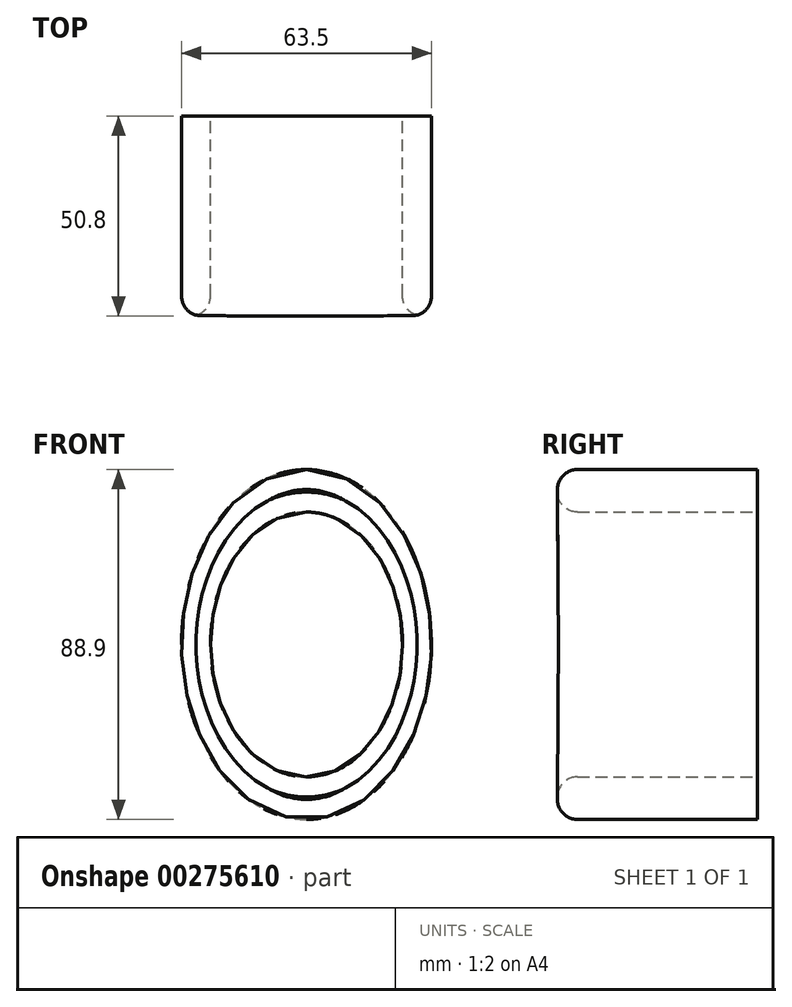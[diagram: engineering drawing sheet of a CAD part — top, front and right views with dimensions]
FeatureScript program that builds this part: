
annotation { "Feature Type Name" : "Feature", "Feature Type Description" : "" }
export const myFeature = defineFeature(function(context is Context, id is Id, definition is map)
    precondition{}
    {
        {
            var Q0;
            Q0=qCreatedBy(makeId("Front.planeOp"),FACE);
            var sketch = newSketch(context, id + "F0", { "sketchPlane" : qUnion([Q0])});
            skEllipse(sketch, "E0", {"center": v(0, 0) * mm, "majorRadius": 44.45 * mm, "minorRadius": 31.75 * mm, "majorAxis": v(0, 1)});
            skEllipse(sketch, "E1", {"center": v(0, 0) * mm, "majorRadius": 33.64 * mm, "minorRadius": 24.39 * mm, "majorAxis": v(0, 1)});
            skSolve(sketch);
        }
        {
            var Q0;
            Q0 = qSketchRegion(id + "F0", true);
            extrude(context, id + "F1", {"entities" : qUnion([Q0]), "depth" : 50.8 * mm});
        }
        {
            var Q0;
            Q0=makeQuery(id+"F1.opExtrude","CAP_EDGE",EDGE,{"disambiguationData":[OSD([sQuery(id+"F0.wireOp",EDGE,"E1")])],"isStart":false});
            var Q1;
            Q1=makeQuery(id+"F1.opExtrude","CAP_FACE",FACE,{"disambiguationData":[OSD([sQuery(id+"F0.wireOp",EDGE,"E0"),sQuery(id+"F0.wireOp",EDGE,"E1")])],"isStart":false});
            fillet(context, id + "F2", {"entities" : qUnion([Q0, Q1]), "radius" : 5.08 * mm, "tangentPropagation" : true, "allowEdgeOverflow" : false});
        }
    });
